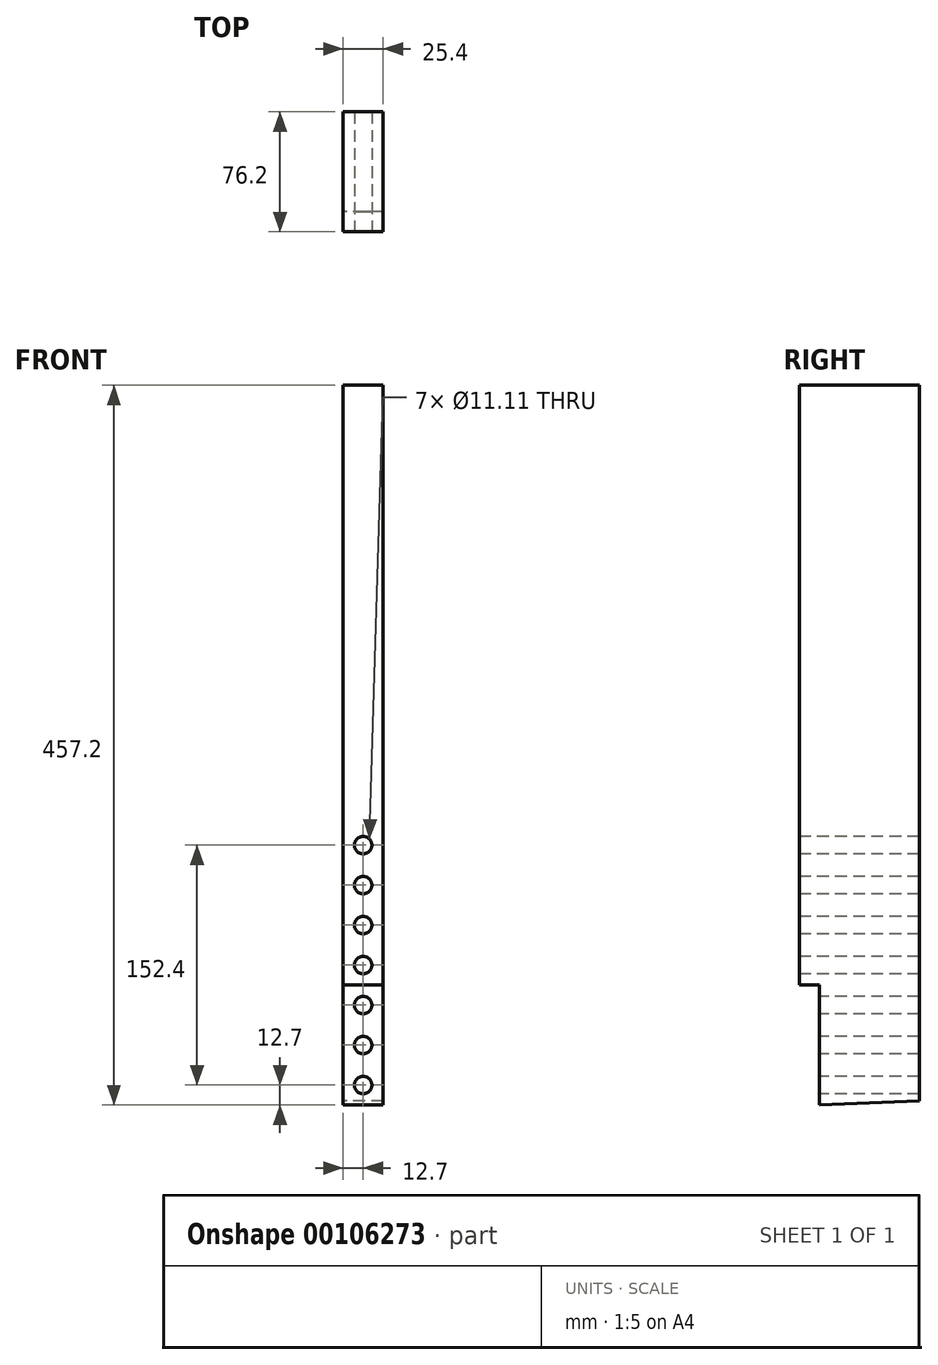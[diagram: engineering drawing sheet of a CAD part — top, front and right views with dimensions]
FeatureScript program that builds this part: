
annotation { "Feature Type Name" : "Feature", "Feature Type Description" : "" }
export const myFeature = defineFeature(function(context is Context, id is Id, definition is map)
    precondition{}
    {
        {
            var Q0;
            Q0=qCreatedBy(makeId("Right.planeOp"),FACE);
            var sketch = newSketch(context, id + "F0", { "sketchPlane" : qUnion([Q0])});
            skLineSegment(sketch, "E0", {"start": v(0, 457.2) * mm, "end": v(0, 76.2) * mm});
            skLineSegment(sketch, "E1", {"start": v(0, 76.2) * mm, "end": v(12.7, 76.2) * mm});
            skLineSegment(sketch, "E2", {"start": v(12.7, 76.2) * mm, "end": v(12.7, 0) * mm});
            skLineSegment(sketch, "E3", {"start": v(12.7, 0) * mm, "end": v(76.2, 2.77) * mm});
            skLineSegment(sketch, "E4", {"start": v(76.2, 2.77) * mm, "end": v(76.2, 457.2) * mm});
            skLineSegment(sketch, "E5", {"start": v(76.2, 457.2) * mm, "end": v(0, 457.2) * mm});
            skLineSegment(sketch, "E6", {"start": v(0, 38.1) * mm, "end": v(89.7, 38.1) * mm, "construction": true});
            skPoint(sketch, "E6.startSnap0", {"position": v(12.7, 38.1) * mm});
            skLineSegment(sketch, "E7", {"start": v(0, 63.5) * mm, "end": v(89.7, 63.5) * mm, "construction": true});
            skLineSegment(sketch, "E8", {"start": v(0, 12.7) * mm, "end": v(89.7, 12.7) * mm, "construction": true});
            skLineSegment(sketch, "E9.bottom", {"start": v(0, 43.66) * mm, "end": v(89.7, 43.66) * mm, "construction": true});
            skLineSegment(sketch, "E9.top", {"start": v(0, 32.54) * mm, "end": v(89.7, 32.54) * mm, "construction": true});
            skLineSegment(sketch, "E9.left", {"start": v(0, 43.66) * mm, "end": v(0, 32.54) * mm, "construction": true});
            skLineSegment(sketch, "E9.right", {"start": v(89.7, 43.66) * mm, "end": v(89.7, 32.54) * mm, "construction": true});
            skLineSegment(sketch, "E10.bottom", {"start": v(0, 69.06) * mm, "end": v(89.7, 69.06) * mm, "construction": true});
            skLineSegment(sketch, "E10.top", {"start": v(0, 57.94) * mm, "end": v(89.7, 57.94) * mm, "construction": true});
            skLineSegment(sketch, "E10.left", {"start": v(0, 69.06) * mm, "end": v(0, 57.94) * mm, "construction": true});
            skLineSegment(sketch, "E10.right", {"start": v(89.7, 69.06) * mm, "end": v(89.7, 57.94) * mm, "construction": true});
            skLineSegment(sketch, "E11.bottom", {"start": v(0, 18.26) * mm, "end": v(89.7, 18.26) * mm, "construction": true});
            skLineSegment(sketch, "E11.top", {"start": v(0, 7.14) * mm, "end": v(89.7, 7.14) * mm, "construction": true});
            skLineSegment(sketch, "E11.left", {"start": v(0, 18.26) * mm, "end": v(0, 7.14) * mm, "construction": true});
            skLineSegment(sketch, "E11.right", {"start": v(89.7, 18.26) * mm, "end": v(89.7, 7.14) * mm, "construction": true});
            skSolve(sketch);
        }
        {
            var Q0;
            Q0=makeQuery(id+"F0.imprint","IMPRINT",FACE,{"disambiguationData":[TD([[makeQuery(id+"F0.imprint","IMPRINT",EDGE,{"derivedFrom":sQuery(id+"F0.wireOp",EDGE,"E0")}),1.0]])]});
            extrude(context, id + "F1", {"entities" : qUnion([Q0]), "endBound" : BoundingType.SYMMETRIC, "depth" : 25.4 * mm});
        }
        {
            var Q0;
            Q0=makeQuery(id+"F1.opExtrude","SWEPT_FACE",FACE,{"disambiguationData":[OSD([sQuery(id+"F0.wireOp",EDGE,"E2")])]});
            var sketch = newSketch(context, id + "F2", { "sketchPlane" : qUnion([Q0])});
            skCircle(sketch, "E12", {"center": v(0, 38.1) * mm, "radius": 5.56 * mm});
            skCircle(sketch, "E13", {"center": v(0, 63.5) * mm, "radius": 5.56 * mm});
            skCircle(sketch, "E14", {"center": v(0, 12.7) * mm, "radius": 5.56 * mm});
            skSolve(sketch);
        }
        {
            var Q0;
            Q0 = qSketchRegion(id + "F2", true);
            extrude(context, id + "F3", {"entities" : qUnion([Q0]), "operationType" : NewBodyOperationType.REMOVE, "endBound" : BoundingType.THROUGH_ALL, "oppositeDirection" : true, "depth" : 25.4 * mm});
        }
        {
            var Q0;
            Q0=makeQuery(id+"F1.opExtrude","SWEPT_FACE",FACE,{"disambiguationData":[OSD([sQuery(id+"F0.wireOp",EDGE,"E0")])]});
            var sketch = newSketch(context, id + "F4", { "sketchPlane" : qUnion([Q0])});
            skCircle(sketch, "E15", {"center": v(0, 114.3) * mm, "radius": 5.56 * mm});
            skCircle(sketch, "E16", {"center": v(0, 139.7) * mm, "radius": 5.56 * mm});
            skCircle(sketch, "E17", {"center": v(0, 88.9) * mm, "radius": 5.56 * mm});
            skCircle(sketch, "E18", {"center": v(0, 165.1) * mm, "radius": 5.56 * mm});
            skSolve(sketch);
        }
        {
            var Q0;
            Q0 = qSketchRegion(id + "F4", true);
            extrude(context, id + "F5", {"entities" : qUnion([Q0]), "operationType" : NewBodyOperationType.REMOVE, "endBound" : BoundingType.THROUGH_ALL, "oppositeDirection" : true, "depth" : 25.4 * mm});
        }
    });
